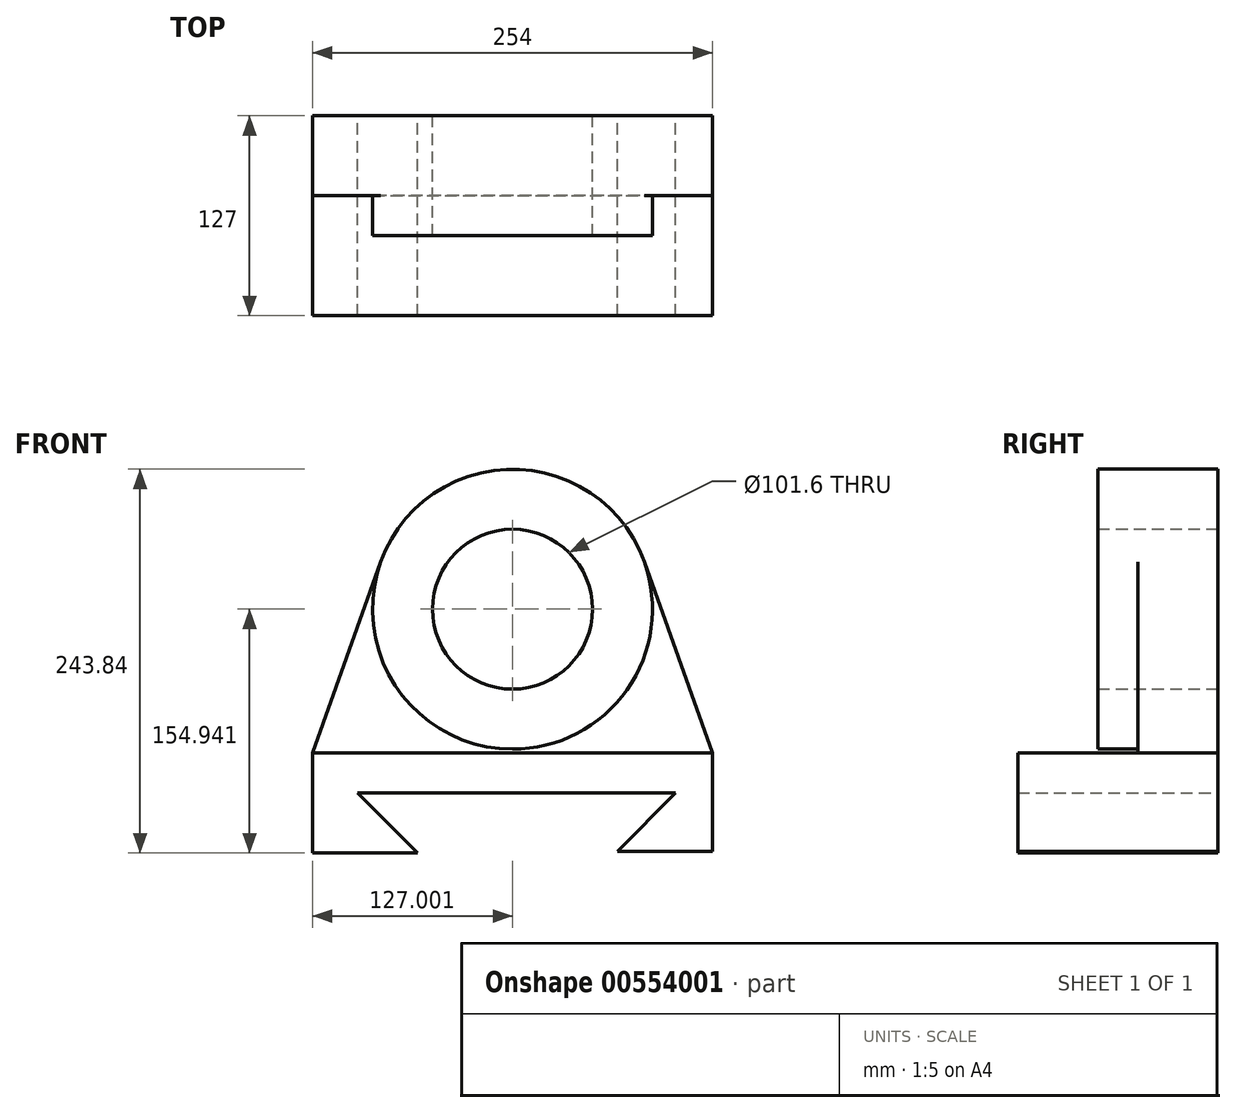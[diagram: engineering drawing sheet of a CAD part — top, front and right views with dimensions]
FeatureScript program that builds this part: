
annotation { "Feature Type Name" : "Feature", "Feature Type Description" : "" }
export const myFeature = defineFeature(function(context is Context, id is Id, definition is map)
    precondition{}
    {
        {
            var Q0;
            Q0=qCreatedBy(makeId("Front.planeOp"),FACE);
            var sketch = newSketch(context, id + "F0", { "sketchPlane" : qUnion([Q0])});
            skLineSegment(sketch, "E0", {"start": v(69.25, -12.44) * mm, "end": v(69.25, 49.9) * mm});
            skLineSegment(sketch, "E1", {"start": v(69.25, 49.9) * mm, "end": v(-184.75, 49.9) * mm});
            skLineSegment(sketch, "E2", {"start": v(-184.75, 49.9) * mm, "end": v(-184.75, -13.6) * mm});
            skCircle(sketch, "E3", {"center": v(-57.75, 141.34) * mm, "radius": 50.8 * mm});
            skCircle(sketch, "E4", {"center": v(-57.75, 141.34) * mm, "radius": 88.9 * mm});
            skLineSegment(sketch, "E5", {"start": v(-118.08, -13.6) * mm, "end": v(-156.18, 24.5) * mm});
            skLineSegment(sketch, "E6", {"start": v(-156.18, 24.5) * mm, "end": v(45.86, 24.5) * mm});
            skLineSegment(sketch, "E7", {"start": v(45.86, 24.5) * mm, "end": v(8.92, -12.44) * mm});
            skLineSegment(sketch, "E8", {"start": v(-118.08, -13.6) * mm, "end": v(-184.75, -13.6) * mm});
            skLineSegment(sketch, "E9", {"start": v(8.92, -12.44) * mm, "end": v(69.25, -12.44) * mm});
            skPoint(sketch, "E10.start.orphan", {"position": v(-118.08, -48.2) * mm});
            skLineSegment(sketch, "E11", {"start": v(-184.75, 49.9) * mm, "end": v(-141.48, 171.2) * mm});
            skLineSegment(sketch, "E12", {"start": v(69.25, 49.9) * mm, "end": v(25.98, 171.2) * mm});
            skSolve(sketch);
        }
        {
            var Q0;
            Q0=makeQuery(id+"F0.imprint","IMPRINT",FACE,{"disambiguationData":[TD([[makeQuery(id+"F0.imprint","IMPRINT",EDGE,{"derivedFrom":sQuery(id+"F0.wireOp",EDGE,"E0")}),1.0]])]});
            extrude(context, id + "F1", {"entities" : qUnion([Q0]), "depth" : 127 * mm, "offsetDistance" : 25.4 * mm});
        }
        {
            var Q0;
            Q0=makeQuery(id+"F0.imprint","IMPRINT",FACE,{"disambiguationData":[TD([[makeQuery(id+"F0.imprint","IMPRINT",EDGE,{"derivedFrom":sQuery(id+"F0.wireOp",EDGE,"E1")}),-1.0]])]});
            var Q1;
            Q1=makeQuery(id+"F0.imprint","IMPRINT",FACE,{"disambiguationData":[TD([[makeQuery(id+"F0.imprint","IMPRINT",EDGE,{"derivedFrom":sQuery(id+"F0.wireOp",EDGE,"E3")}),-1.0]])]});
            extrude(context, id + "F2", {"entities" : qUnion([Q0, Q1]), "operationType" : NewBodyOperationType.ADD, "depth" : 50.8 * mm, "offsetDistance" : 25.4 * mm});
        }
        {
            var Q0;
            Q0=makeQuery(id+"F0.imprint","IMPRINT",FACE,{"disambiguationData":[TD([[makeQuery(id+"F0.imprint","IMPRINT",EDGE,{"derivedFrom":sQuery(id+"F0.wireOp",EDGE,"E3")}),-1.0]])]});
            extrude(context, id + "F3", {"entities" : qUnion([Q0]), "operationType" : NewBodyOperationType.ADD, "depth" : 76.2 * mm, "offsetDistance" : 25.4 * mm});
        }
    });
